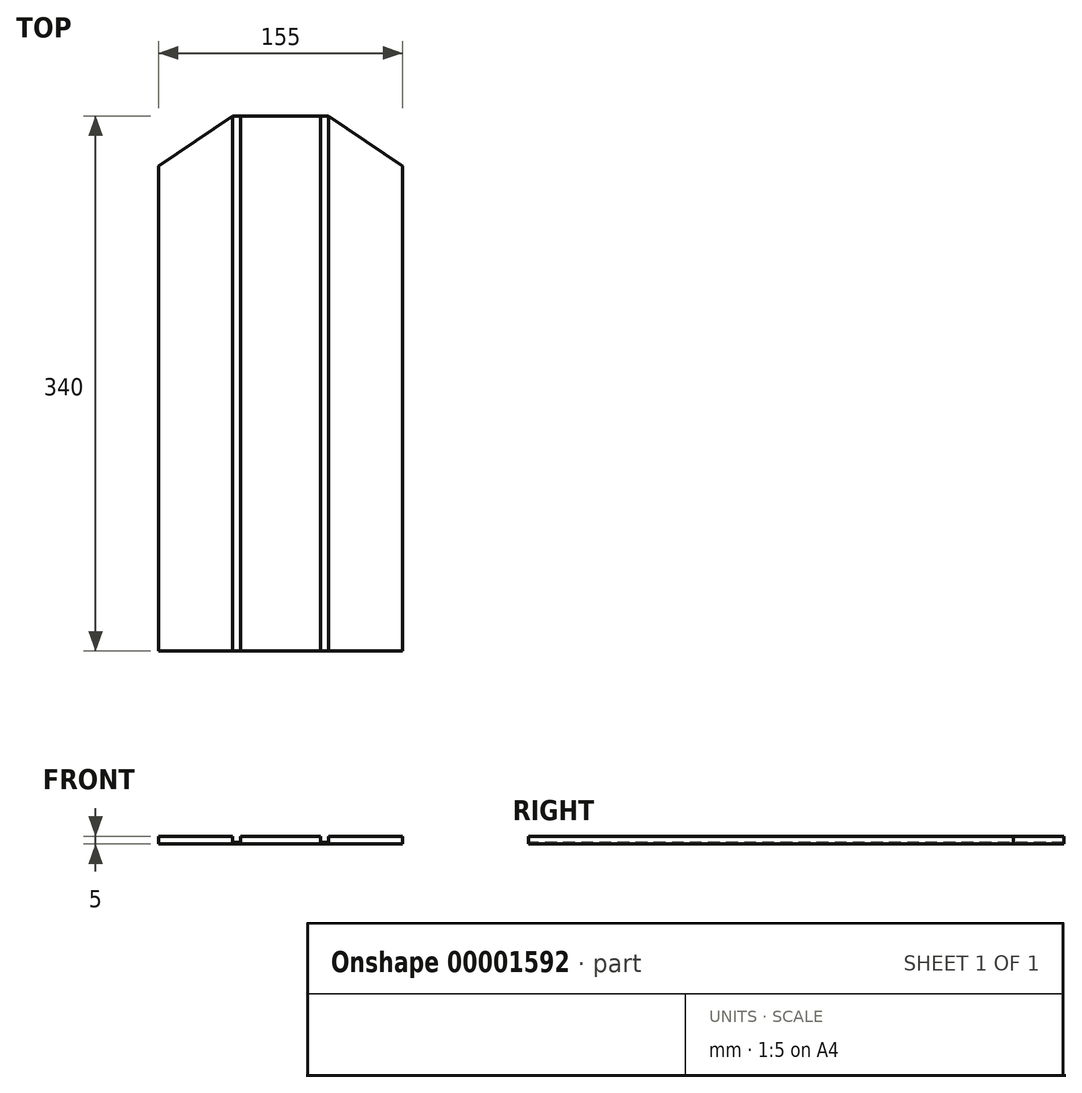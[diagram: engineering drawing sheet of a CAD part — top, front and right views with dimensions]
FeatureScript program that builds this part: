
annotation { "Feature Type Name" : "Feature", "Feature Type Description" : "" }
export const myFeature = defineFeature(function(context is Context, id is Id, definition is map)
    precondition{}
    {
        {
            var Q0;
            Q0=qCreatedBy(makeId("Top.planeOp"),FACE);
            var sketch = newSketch(context, id + "F0", { "sketchPlane" : qUnion([Q0])});
            skLineSegment(sketch, "E0", {"start": v(0, 0) * mm, "end": v(-30.5, 0) * mm});
            skLineSegment(sketch, "E1", {"start": v(-30.5, 0) * mm, "end": v(-77.5, 0) * mm});
            skLineSegment(sketch, "E2", {"start": v(-77.5, 0) * mm, "end": v(-77.5, 308) * mm});
            skLineSegment(sketch, "E3", {"start": v(-77.5, 308) * mm, "end": v(-30.5, 340) * mm});
            skLineSegment(sketch, "E4", {"start": v(-30.5, 340) * mm, "end": v(0, 340) * mm});
            skLineSegment(sketch, "E5", {"start": v(0, 340) * mm, "end": v(30.5, 340) * mm});
            skLineSegment(sketch, "E6", {"start": v(30.5, 340) * mm, "end": v(77.5, 308) * mm});
            skLineSegment(sketch, "E7", {"start": v(77.5, 308) * mm, "end": v(77.5, 0) * mm});
            skLineSegment(sketch, "E8", {"start": v(77.5, 0) * mm, "end": v(30.5, 0) * mm});
            skLineSegment(sketch, "E9", {"start": v(30.5, 0) * mm, "end": v(0, 0) * mm});
            skLineSegment(sketch, "E10", {"start": v(30.5, 340) * mm, "end": v(30.5, 0) * mm});
            skLineSegment(sketch, "E11", {"start": v(25.5, 340) * mm, "end": v(25.5, 0) * mm});
            skLineSegment(sketch, "E12", {"start": v(-30.5, 340) * mm, "end": v(-30.5, 0) * mm});
            skLineSegment(sketch, "E13", {"start": v(-25.5, 340) * mm, "end": v(-25.5, 0) * mm});
            skSolve(sketch);
        }
        {
            var Q0;
            {var subQ1=sQuery(id+"F0.wireOp",EDGE,"E12");Q0=makeQuery(id+"F0.imprint","IMPRINT",FACE,{"disambiguationData":[TD([[makeQuery(id+"F0.imprint","IMPRINT",EDGE,{"derivedFrom":subQ1}),1.0]])]});}
            var Q1;
            {var subQ0=sQuery(id+"F0.wireOp",EDGE,"E10");Q1=makeQuery(id+"F0.imprint","IMPRINT",FACE,{"disambiguationData":[TD([[makeQuery(id+"F0.imprint","IMPRINT",EDGE,{"derivedFrom":subQ0}),-1.0]])]});}
            extrude(context, id + "F1", {"entities" : qUnion([Q0, Q1]), "depth" : 1 * mm});
        }
        {
            var Q0;
            Q0=makeQuery(id+"F0.imprint","IMPRINT",FACE,{"disambiguationData":[TD([[makeQuery(id+"F0.imprint","IMPRINT",EDGE,{"derivedFrom":sQuery(id+"F0.wireOp",EDGE,"E6")}),-1.0]])]});
            var Q1;
            {var subQ1=sQuery(id+"F0.wireOp",EDGE,"E11");Q1=makeQuery(id+"F0.imprint","IMPRINT",FACE,{"disambiguationData":[TD([[makeQuery(id+"F0.imprint","IMPRINT",EDGE,{"derivedFrom":subQ1}),-1.0]])]});}
            var Q2;
            Q2=makeQuery(id+"F0.imprint","IMPRINT",FACE,{"disambiguationData":[TD([[makeQuery(id+"F0.imprint","IMPRINT",EDGE,{"derivedFrom":sQuery(id+"F0.wireOp",EDGE,"E1")}),-1.0]])]});
            extrude(context, id + "F2", {"entities" : qUnion([Q0, Q1, Q2]), "depth" : 5 * mm});
        }
    });
